FCSTD DOCUMENT  (FreeCAD 0.19R24267 (Git))
Label: pattern
License: All rights reserved
LicenseURL: http://en.wikipedia.org/wiki/All_rights_reserved
objects: Sketcher::SketchObject×3
note: 3 computed .brp shape members not serialized (recipe doc carries the construction recipe); baked Part::Feature solids carry a one-line shape summary decoded from their .brp

FEATURE [Sketcher::SketchObject] Sketch
  FullyConstrained = true
  MapMode = 5
  sketch-geometry (3):
    g0: ArcOfCircle CenterX=0 CenterY=0 CenterZ=0 NormalX=0 NormalY=0 NormalZ=1 AngleXU=0 Radius=30 StartAngle=4.81711 EndAngle=10.8909
    g1: LineSegment StartX=-3.13585 StartY=-29.8357 StartZ=0 EndX=0 EndY=0 EndZ=0
    g2: LineSegment StartX=0 StartY=0 StartZ=0 EndX=3.13585 EndY=-29.8357 EndZ=0
  constraints (8):
    c: Coincident(g0,g-1)
    c: Coincident(g1,g0)
    c: Coincident(g1,g-1)
    c: Coincident(g2,g1)
    c: Coincident(g2,g0)
    c: Radius(g0) = 30
    c: Symmetric(g1,g2,g-2)
    c: Angle(g-2,g1) = 3.03687
FEATURE [Sketcher::SketchObject] Sketch001
  FullyConstrained = false
  MapMode = 47
  Placement = pos=(-3.13585,-29.8357,0) rot=(0.57735,0.57735,0.57735;2.0944rad)
  Support = -> [Sketch]
  sketch-geometry (1):
    g0: LineSegment StartX=0 StartY=0 StartZ=0 EndX=0 EndY=32.8652 EndZ=0
  constraints (2):
    c: Coincident(g0,g-1)
    c: PointOnObject(g0,g-2)
FEATURE [Sketcher::SketchObject] Sketch002
  ExternalGeometry = -> [Sketch001,Sketch]
  FullyConstrained = false
  MapMode = 13
  Placement = pos=(-1.04528,-29.8357,10.9551) rot=(1,0,0;1.5708rad)
  Support = -> [Sketch,Sketch001]
  sketch-geometry (15):
    g0: LineSegment StartX=4.18114 StartY=-10.9551 StartZ=0 EndX=4.18114 EndY=21.9101 EndZ=0
    g1: LineSegment StartX=2.75413 StartY=-7.89334 StartZ=0 EndX=2.41178 EndY=-8.63248 EndZ=0
    g2: LineSegment StartX=2.41178 StartY=-8.63248 StartZ=0 EndX=2.88072 EndY=-9.29853 EndZ=0
    g3: LineSegment StartX=2.88072 StartY=-9.29853 StartZ=0 EndX=3.69201 EndY=-9.22545 EndZ=0
    g4: LineSegment StartX=3.69201 StartY=-9.22545 StartZ=0 EndX=4.03436 EndY=-8.48631 EndZ=0
    g5: LineSegment StartX=4.03436 StartY=-8.48631 StartZ=0 EndX=3.56542 EndY=-7.82025 EndZ=0
    g6: LineSegment StartX=3.56542 StartY=-7.82025 StartZ=0 EndX=2.75413 EndY=-7.89334 EndZ=0
    g7: Circle CenterX=3.22307 CenterY=-8.55939 CenterZ=0 NormalX=0 NormalY=0 NormalZ=1 AngleXU=0 Radius=0.814574
    g8: LineSegment StartX=-1.82493 StartY=-4.22743 StartZ=0 EndX=-1.66911 EndY=-5.73026 EndZ=0
    g9: LineSegment StartX=-1.66911 StartY=-5.73026 StartZ=0 EndX=-0.28971 EndY=-6.34673 EndZ=0
    g10: LineSegment StartX=-0.28971 StartY=-6.34673 StartZ=0 EndX=0.933873 EndY=-5.46038 EndZ=0
    g11: LineSegment StartX=0.933873 StartY=-5.46038 StartZ=0 EndX=0.778056 EndY=-3.95754 EndZ=0
    g12: LineSegment StartX=0.778056 StartY=-3.95754 StartZ=0 EndX=-0.601344 EndY=-3.34107 EndZ=0
    g13: LineSegment StartX=-0.601344 StartY=-3.34107 StartZ=0 EndX=-1.82493 EndY=-4.22743 EndZ=0
    g14: Circle CenterX=-0.445527 CenterY=-4.8439 CenterZ=0 NormalX=0 NormalY=0 NormalZ=1 AngleXU=0 Radius=1.51089
  constraints (29):
    c: Coincident(g0,g-5)
    c: Vertical(g0)
    c: Equal(g-6,g0)
    c: Coincident(g1,g2)
    c: Coincident(g2,g3)
    c: Coincident(g3,g4)
    c: Coincident(g4,g5)
    c: Coincident(g5,g6)
    c: Coincident(g6,g1)
    c: Equal(g1, g2-g6) x5
    c: PointOnObject(g1,g7)
    c: PointOnObject(g2,g7)
    c: PointOnObject(g3,g7)
    c: PointOnObject(g4,g7)
    c: PointOnObject(g5,g7)
    c: PointOnObject(g6,g7)
    c: Coincident(g8,g9)
    c: Coincident(g9,g10)
    c: Coincident(g10,g11)
    c: Coincident(g11,g12)
    c: Coincident(g12,g13)
    c: Coincident(g13,g8)
    c: Equal(g8, g9-g13) x5
    c: PointOnObject(g8,g14)
    c: PointOnObject(g9,g14)
    c: PointOnObject(g10,g14)
    c: PointOnObject(g11,g14)
    c: PointOnObject(g12,g14)
    c: PointOnObject(g13,g14)
